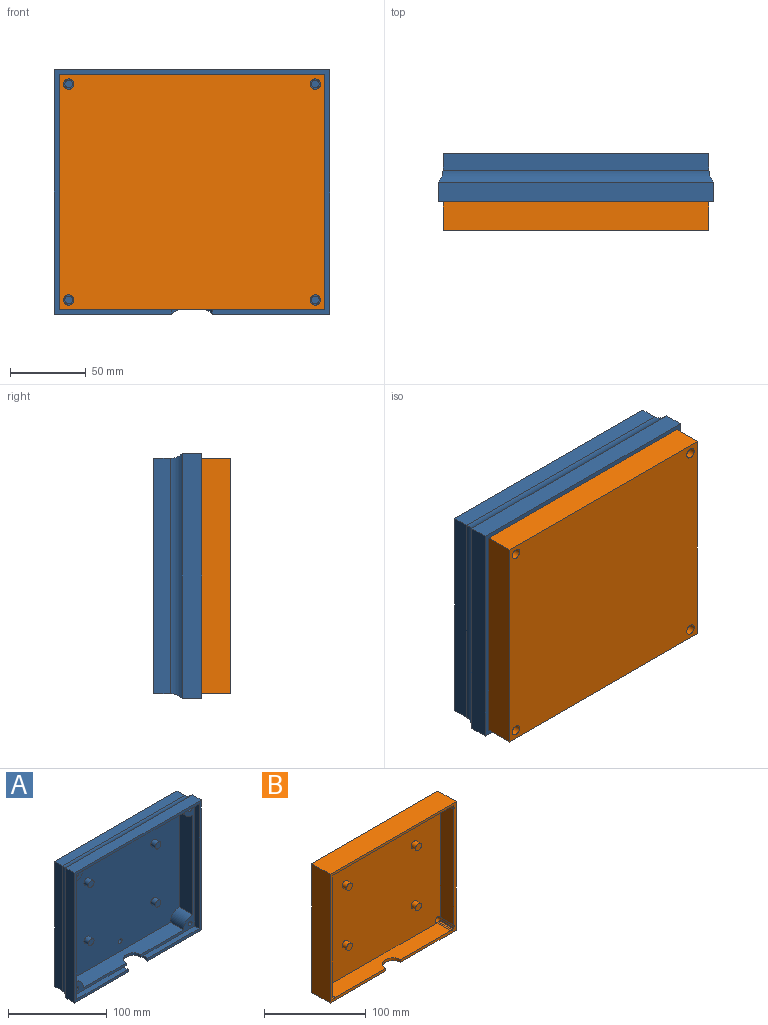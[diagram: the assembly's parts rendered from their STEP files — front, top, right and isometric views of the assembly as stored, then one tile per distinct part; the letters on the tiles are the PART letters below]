
ASSEMBLY  parts=2 mates=1
PART A: 52 faces, bbox 181.6x31.8x161.3 mm
  f0: plane 74.34x6.35mm, normal (0,0,1), area 465.9mm2, adj f2,f10,f20,f45
  f1: plane 74.34x6.35mm, normal (0,0,1), area 465.9mm2, adj f2,f10,f21,f44
  f2: plane 181.61x161.29mm, normal (0,-1,0), area 2052.7mm2, adj f0,f1,f3,f4,f19,f20,f21,f27
  f3: plane 77.51x12.7mm, normal (0,0,-1), area 972.1mm2, adj f2,f29,f45,f47
  f4: plane 77.51x12.7mm, normal (0,0,-1), area 972.1mm2, adj f2,f27,f44,f51
  f5: plane 143.43x19.05mm, normal (0,0,1), area 2560mm2, adj f6,f10,f32,f33,f46
  f6: plane 168.83x148.77mm, normal (0,-1,0), area 24363.5mm2, adj f5,f7,f8,f9,f11,f12,f13,f14
  f7: plane 123.37x19.05mm, normal (1,0,0), area 2350.2mm2, adj f6,f10,f31,f32
  f8: plane 123.37x19.05mm, normal (-1,0,0), area 2350.2mm2, adj f6,f10,f30,f33
  f9: plane 143.43x19.05mm, normal (0,0,-1), area 2732.4mm2, adj f6,f10,f30,f31
  f10: plane 175.26x154.94mm, normal (0,-1,0), area 2397.9mm2, adj f0,f1,f5,f7,f8,f9,f19,f20
  f11: cylinder r=4.05mm len=8.1mm, axis (0,-1,0), area 161.6mm2, adj f6,f18
  f12: cylinder r=4.05mm len=8.1mm, axis (0,-1,0), area 161.6mm2, adj f6,f17
  f13: cylinder r=4.05mm len=8.1mm, axis (0,-1,0), area 161.6mm2, adj f6,f16
  f14: cylinder r=4.05mm len=8.1mm, axis (0,-1,0), area 161.6mm2, adj f6,f15
  f15: plane 8.1x8.1mm, normal (0,-1,0), area 51.6mm2, adj f14
  f16: plane 8.1x8.1mm, normal (0,-1,0), area 51.6mm2, adj f13
  f17: plane 8.1x8.1mm, normal (0,-1,0), area 51.6mm2, adj f12
  f18: plane 8.1x8.1mm, normal (0,-1,0), area 51.6mm2, adj f11
  f19: plane 175.26x6.35mm, normal (0,0,-1), area 1112.9mm2, adj f2,f10,f20,f21
  f20: plane 154.94x6.35mm, normal (-1,0,0), area 983.9mm2, adj f0,f2,f10,f19
  f21: plane 154.94x6.35mm, normal (1,0,0), area 983.9mm2, adj f1,f2,f10,f19
  f22: plane 175.26x154.94mm, normal (0,1,0), area 27114.2mm2, adj f23,f24,f25,f26,f42,f43
  f23: plane 154.94x11.14mm, normal (1,0,0), area 1726.7mm2, adj f22,f24,f26,f48
  f24: plane 175.26x25.4mm, normal (0,0,-1), area 2119.3mm2, adj f10,f22,f23,f25,f44,f45,f46,f47
  f25: plane 154.94x11.14mm, normal (-1,0,0), area 1726.7mm2, adj f22,f24,f26,f50
  f26: plane 175.26x11.14mm, normal (0,0,1), area 1953.2mm2, adj f22,f23,f25,f49
  f27: plane 161.29x12.7mm, normal (-1,0,0), area 2048.4mm2, adj f2,f4,f28,f50
  f28: plane 181.61x12.7mm, normal (0,0,1), area 2306.4mm2, adj f2,f27,f29,f49
  f29: plane 161.29x12.7mm, normal (1,0,0), area 2048.4mm2, adj f2,f3,f28,f48
  f30: cylinder r=12.7mm len=19.05mm, axis (0,1,0), area 380mm2, adj f6,f8,f9,f10
  f31: cylinder r=12.7mm len=19.05mm, axis (0,1,0), area 380mm2, adj f6,f7,f9,f10
  f32: cylinder r=12.7mm len=19.05mm, axis (0,1,0), area 380mm2, adj f5,f6,f7,f10
  f33: cylinder r=12.7mm len=19.05mm, axis (0,1,0), area 380mm2, adj f5,f6,f8,f10
  f34: cylinder r=2.55mm len=19.05mm, axis (0,-1,0), area 305.5mm2, adj f10,f35
  f35: plane 5.11x5.11mm, normal (0,-1,0), area 20.5mm2, adj f34
  f36: cylinder r=2.55mm len=19.05mm, axis (0,-1,0), area 305.5mm2, adj f10,f37
  f37: plane 5.11x5.11mm, normal (0,-1,0), area 20.5mm2, adj f36
  f38: cylinder r=2.55mm len=19.05mm, axis (0,-1,0), area 305.5mm2, adj f10,f39
  f39: plane 5.11x5.11mm, normal (0,-1,0), area 20.5mm2, adj f38
  f40: cylinder r=2.55mm len=19.05mm, axis (0,-1,0), area 305.5mm2, adj f10,f41
  f41: plane 5.11x5.11mm, normal (0,-1,0), area 20.5mm2, adj f40
  f42: cylinder r=2.54mm len=6.35mm, axis (0,-1,0), area 101.3mm2, adj f6,f22
  f43: cylinder r=2.54mm len=6.35mm, axis (0,-1,0), area 101.3mm2, adj f6,f22
  f44: cylinder r=14.73mm len=20.61mm, axis (0,0,-1), area 51.4mm2, adj f1,f2,f4,f24,f51
  f45: cylinder r=14.73mm len=20.61mm, axis (0,0,-1), area 51.4mm2, adj f0,f2,f3,f24,f47
  f46: cylinder r=10.48mm len=20.96mm, axis (0,0,-1), area 101.6mm2, adj f5,f10,f24
  f47: cylinder r=11.43mm len=87.09mm, axis (-1,0,0), area 685.7mm2, adj f3,f24,f45,f48
  f48: cylinder r=11.43mm len=161.29mm, axis (0,0,-1), area 1371.5mm2, adj f23,f29,f47,f49
  f49: cylinder r=11.43mm len=181.61mm, axis (-1,0,0), area 1548.9mm2, adj f26,f28,f48,f50
  f50: cylinder r=11.43mm len=161.29mm, axis (0,0,-1), area 1371.5mm2, adj f25,f27,f49,f51
  f51: cylinder r=11.43mm len=87.09mm, axis (-1,0,0), area 685.7mm2, adj f4,f24,f44,f50
PART B: 36 faces, bbox 175.3x25.4x154.9 mm
  f0: plane 175.26x154.94mm, normal (0,-1,0), area 1970mm2, adj f1,f2,f3,f4,f5,f6,f7,f8
  f1: plane 139.47x19.05mm, normal (-1,0,0), area 2656.9mm2, adj f0,f12,f33,f34
  f2: plane 19.05x1.88mm, normal (-1,0,0), area 35.8mm2, adj f0,f3,f10,f33
  f3: plane 19.05x2.09mm, normal (0,0,-1), area 39.7mm2, adj f0,f2,f10,f33
  f4: plane 160.46x19.05mm, normal (0,0,-1), area 3056.7mm2, adj f0,f12,f32,f33
  f5: plane 19.05x1.88mm, normal (1,0,0), area 35.8mm2, adj f0,f11,f23,f32
  f6: plane 139.47x19.05mm, normal (1,0,0), area 2656.9mm2, adj f0,f12,f31,f32
  f7: plane 19.05x2.09mm, normal (0,0,1), area 39.7mm2, adj f0,f9,f22,f34
  f8: plane 160.46x19.05mm, normal (0,0,1), area 2884.3mm2, adj f0,f12,f31,f34,f35
  f9: plane 2.09x1.88mm, normal (0,-1,0), area 1.4mm2, adj f7,f22,f34
  f10: plane 2.09x1.88mm, normal (0,-1,0), area 1.4mm2, adj f2,f3,f33
  f11: plane 2.09x1.88mm, normal (0,-1,0), area 1.4mm2, adj f5,f23,f32
  f12: plane 168.83x148.77mm, normal (0,-1,0), area 24760.6mm2, adj f1,f4,f6,f8,f13,f14,f15,f16
  f13: cylinder r=4.05mm len=8.1mm, axis (0,-1,0), area 161.6mm2, adj f12,f30
  f14: cylinder r=4.05mm len=8.1mm, axis (0,-1,0), area 161.6mm2, adj f12,f29
  f15: cylinder r=4.05mm len=8.1mm, axis (0,-1,0), area 161.6mm2, adj f12,f28
  f16: cylinder r=4.05mm len=8.1mm, axis (0,-1,0), area 161.6mm2, adj f12,f27
  f17: plane 154.94x25.4mm, normal (1,0,0), area 3935.5mm2, adj f0,f18,f20,f21
  f18: plane 175.26x25.4mm, normal (0,0,1), area 4451.6mm2, adj f0,f17,f19,f21
  f19: plane 154.94x25.4mm, normal (-1,0,0), area 3935.5mm2, adj f0,f18,f20,f21
  f20: plane 175.26x25.4mm, normal (0,0,-1), area 4279.2mm2, adj f0,f17,f19,f21,f35
  f21: plane 175.26x154.94mm, normal (0,1,0), area 27007mm2, adj f17,f18,f19,f20,f31,f32,f33,f34
  f22: plane 19.05x1.88mm, normal (-1,0,0), area 35.8mm2, adj f0,f7,f9,f34
  f23: plane 19.05x2.09mm, normal (0,0,-1), area 39.7mm2, adj f0,f5,f11,f32
  f24: plane 19.05x1.88mm, normal (1,0,0), area 35.8mm2, adj f0,f25,f26,f31
  f25: plane 19.05x2.09mm, normal (0,0,1), area 39.7mm2, adj f0,f24,f26,f31
  f26: plane 2.09x1.88mm, normal (0,-1,0), area 1.4mm2, adj f24,f25,f31
  f27: plane 8.1x8.1mm, normal (0,-1,0), area 51.6mm2, adj f16
  f28: plane 8.1x8.1mm, normal (0,-1,0), area 51.6mm2, adj f15
  f29: plane 8.1x8.1mm, normal (0,-1,0), area 51.6mm2, adj f14
  f30: plane 8.1x8.1mm, normal (0,-1,0), area 51.6mm2, adj f13
  f31: cylinder r=3.43mm len=25.4mm, axis (0,1,0), area 231.8mm2, adj f0,f6,f8,f12,f21,f24,f25,f26
  f32: cylinder r=3.43mm len=25.4mm, axis (0,1,0), area 231.8mm2, adj f0,f4,f5,f6,f11,f12,f21,f23
  f33: cylinder r=3.43mm len=25.4mm, axis (0,1,0), area 231.8mm2, adj f0,f1,f2,f3,f4,f10,f12,f21
  f34: cylinder r=3.43mm len=25.4mm, axis (0,1,0), area 231.8mm2, adj f0,f1,f7,f8,f9,f12,f21,f22
  f35: cylinder r=10.48mm len=20.96mm, axis (0,0,-1), area 101.6mm2, adj f0,f8,f20
PLACE A t=(56.69,92.32,65.58)mm
PLACE B rot(axis=(0,0,-1),180deg) t=(56.69,41.52,65.58)mm
MATE fastened B.f0 <-> A.f10  axis (0,1,0) through (-30.94,66.92,143.05)mm
